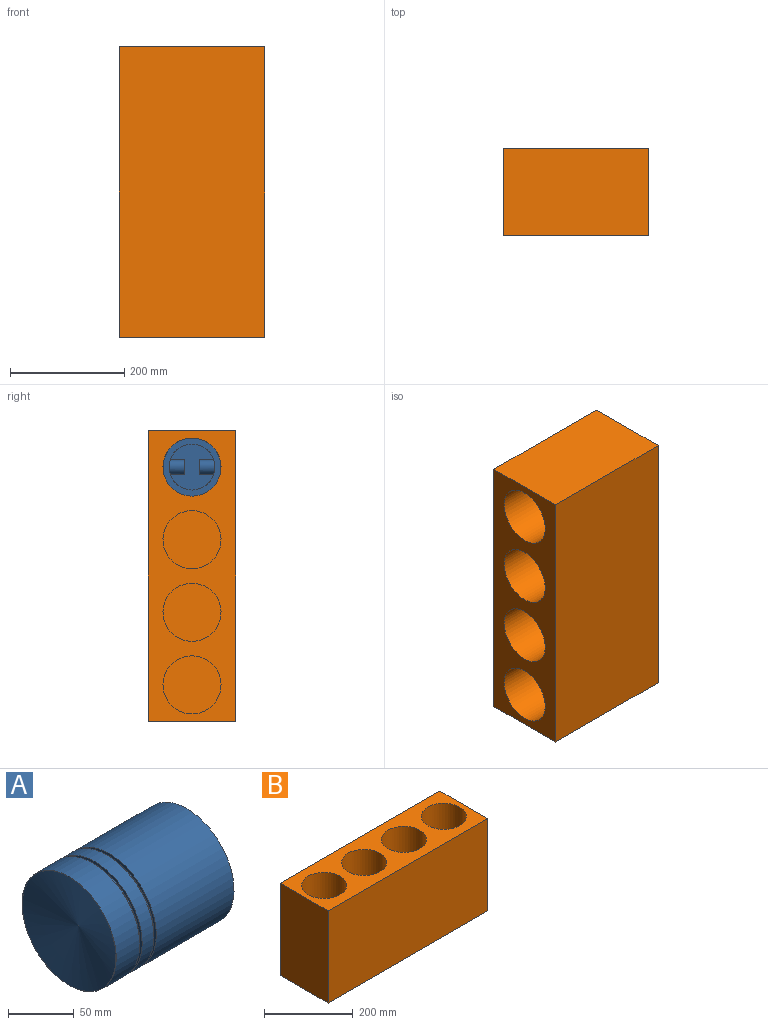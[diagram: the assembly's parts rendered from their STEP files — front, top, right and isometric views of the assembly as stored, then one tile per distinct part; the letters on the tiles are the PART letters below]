
ASSEMBLY  parts=2 mates=1
PART A: 27 faces, bbox 127x101.6x101.6 mm
  f0: plane 25.43x12.7mm, normal (0,0,1), area 322.9mm2, adj f2,f4,f16,f20
  f1: plane 25.43x12.7mm, normal (0,0,-1), area 322.9mm2, adj f2,f3,f16,f20
  f2: cylinder r=12.7mm len=27.49mm, axis (0,1,0), area 1055.8mm2, adj f0,f1,f3,f4,f20
  f3: cylinder r=40.19mm len=80.37mm, axis (1,0,0), area 2621.8mm2, adj f1,f2,f8,f16,f18,f19
  f4: cylinder r=40.19mm len=80.37mm, axis (1,0,0), area 2621.8mm2, adj f0,f2,f8,f16,f17,f18
  f5: plane 101.6x101.6mm, normal (1,0,0), area 790.5mm2, adj f6,f15
  f6: cylinder r=50.8mm len=101.6mm, axis (-1,0,0), area 8107.3mm2, adj f5,f7
  f7: plane 101.6x101.6mm, normal (-1,0,0), area 85mm2, adj f6,f26
  f8: plane 101.6x101.6mm, normal (1,0,0), area 3034mm2, adj f3,f4,f9
  f9: cylinder r=50.8mm len=101.6mm, axis (-1,0,0), area 26754.2mm2, adj f8,f10
  f10: plane 101.6x101.6mm, normal (-1,0,0), area 790.5mm2, adj f9,f11
  f11: cylinder r=48.26mm len=96.52mm, axis (-1,0,0), area 770.2mm2, adj f10,f12
  f12: plane 101.6x101.6mm, normal (1,0,0), area 790.5mm2, adj f11,f13
  f13: cylinder r=50.8mm len=101.6mm, axis (-1,0,0), area 4053.7mm2, adj f12,f14
  f14: plane 101.6x101.6mm, normal (-1,0,0), area 790.5mm2, adj f13,f15
  f15: cylinder r=48.26mm len=96.52mm, axis (-1,0,0), area 770.2mm2, adj f5,f14
  f16: plane 80.37x76.25mm, normal (1,0,0), area 3711.5mm2, adj f0,f1,f3,f4,f17,f19,f20,f21
  f17: plane 25.43x12.7mm, normal (0,0,1), area 322.9mm2, adj f4,f16,f18,f21
  f18: cylinder r=12.7mm len=27.49mm, axis (0,1,0), area 1055.8mm2, adj f3,f4,f17,f19,f21
  f19: plane 25.43x12.7mm, normal (0,0,-1), area 322.9mm2, adj f3,f16,f18,f21
  f20: plane 25.4x25.4mm, normal (0,-1,0), area 449.3mm2, adj f0,f1,f2,f16,f22
  f21: plane 25.4x25.4mm, normal (0,1,0), area 449.3mm2, adj f16,f17,f18,f19,f25
  f22: cylinder r=6.35mm len=27.49mm, axis (0,1,0), area 1086.5mm2, adj f20,f23
  f23: cylinder r=40.19mm len=12.7mm, axis (1,0,0), area 127.1mm2, adj f22
  f24: cylinder r=40.19mm len=12.7mm, axis (1,0,0), area 127.1mm2, adj f25
  f25: cylinder r=6.35mm len=27.49mm, axis (0,1,0), area 1086.6mm2, adj f21,f24
  f26: cone r=50.53mm half-angle=78.9deg, axis (-1,0,0), area 8174.5mm2, adj f7
PART B: 14 faces, bbox 508x152.4x254 mm
  f0: plane 254x152.4mm, normal (-1,0,0), area 38709.6mm2, adj f1,f3,f4,f5
  f1: plane 508x254mm, normal (0,-1,0), area 129032mm2, adj f0,f2,f4,f5
  f2: plane 254x152.4mm, normal (1,0,0), area 38709.6mm2, adj f1,f3,f4,f5
  f3: plane 508x254mm, normal (0,1,0), area 129032mm2, adj f0,f2,f4,f5
  f4: plane 508x152.4mm, normal (0,0,-1), area 77419.2mm2, adj f0,f1,f2,f3
  f5: plane 508x152.4mm, normal (0,0,1), area 44989.9mm2, adj f0,f1,f2,f3,f6,f8,f10,f12
  f6: cylinder r=50.8mm len=228.6mm, axis (0,0,1), area 72965.9mm2, adj f5,f7
  f7: plane 101.6x101.6mm, normal (0,0,1), area 8107.3mm2, adj f6
  f8: cylinder r=50.8mm len=228.6mm, axis (0,0,1), area 72965.9mm2, adj f5,f9
  f9: plane 101.6x101.6mm, normal (0,0,1), area 8107.3mm2, adj f8
  f10: cylinder r=50.8mm len=228.6mm, axis (0,0,1), area 72965.9mm2, adj f5,f11
  f11: plane 101.6x101.6mm, normal (0,0,1), area 8107.3mm2, adj f10
  f12: cylinder r=50.8mm len=228.6mm, axis (0,0,1), area 72965.9mm2, adj f5,f13
  f13: plane 101.6x101.6mm, normal (0,0,1), area 8107.3mm2, adj f12
PLACE A rot(axis=(0,0,-1),180deg) t=(50.65,-116.52,329.34)mm
PLACE B rot(axis=(0.71,0,-0.71),180deg) t=(-176.23,-116.52,138.84)mm
MATE slider A.f3 <-> B.f10  axis (-1,0,0) through (-50.95,-116.52,329.34)mm
